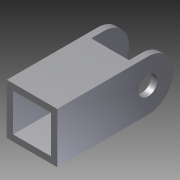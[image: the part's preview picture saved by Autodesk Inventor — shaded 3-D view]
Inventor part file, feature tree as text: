
AUTODESK INVENTOR PART (.ipt)
format: ipt  version: 2012 (Build 160160000, 160)  size: 120,320 bytes
history: native  units: in
note: dims shown in document units (in); Inventor stores cm internally (conversion verified against a paired STEP export)
features: extrude x3, sketch x3
ambient origin geometry x8: Origin, YZ Plane, XZ Plane, XY Plane, X Axis, Y Axis, Z Axis, Center Point
bodies: Solid1 (feature_tree)
feature tree (6):
  extrude  "Extrusion1"  Depth=1.0in
  extrude  "Extrusion2"  Depth=0.125in
  extrude  "Extrusion3"  Depth=0.125in
  sketch  "Sketch1"  dims[d0=1.0in d1=1.0in]
  sketch  "Sketch2"  dims[d2=0.125in d3=0.125in]
  sketch  "Sketch3"  dims[d4=0.125in d5=0.125in d6=2.3in d7=0.0in d8=0.375in d9=0.5in d10=0.5in d11=1.0in d12=0.0in d13=0.75in d14=0.125in d15=1.0in d16=0.0in d17=0.625in d18=0.25in]
